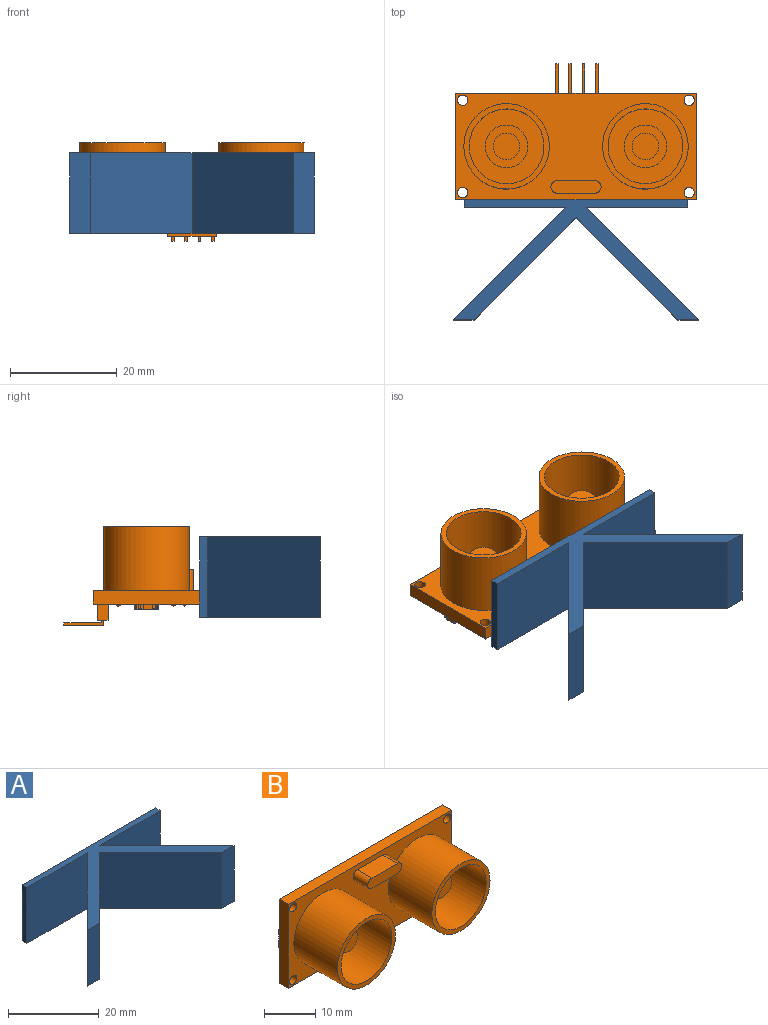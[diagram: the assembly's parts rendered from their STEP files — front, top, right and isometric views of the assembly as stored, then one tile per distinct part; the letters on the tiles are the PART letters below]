
ASSEMBLY  parts=2 mates=1
PART A: 13 faces, bbox 45.8x22.5x15.1 mm
  f0: plane 19.09x19.09mm, normal (0.71,-0.71,0), area 408mm2, adj f1,f10,f11,f12
  f1: plane 19.09x19.09mm, normal (-0.71,-0.71,0), area 408mm2, adj f0,f2,f11,f12
  f2: plane 15.11x3.82mm, normal (0,-1,0), area 57.7mm2, adj f1,f3,f11,f12
  f3: plane 21x21mm, normal (0.71,0.71,0), area 448.8mm2, adj f2,f4,f11,f12
  f4: plane 18.94x15.11mm, normal (0,-1,0), area 286.2mm2, adj f3,f5,f11,f12
  f5: plane 15.11x1.5mm, normal (1,0,0), area 22.7mm2, adj f4,f6,f11,f12
  f6: plane 41.7x15.11mm, normal (0,1,0), area 630.1mm2, adj f5,f7,f11,f12
  f7: plane 15.11x1.5mm, normal (-1,0,0), area 22.7mm2, adj f6,f8,f11,f12
  f8: plane 18.94x15.11mm, normal (0,-1,0), area 286.2mm2, adj f7,f9,f11,f12
  f9: plane 21x21mm, normal (-0.71,0.71,0), area 448.8mm2, adj f8,f10,f11,f12
  f10: plane 15.11x3.82mm, normal (0,-1,0), area 57.7mm2, adj f0,f9,f11,f12
  f11: plane 45.82x22.5mm, normal (0,0,1), area 219.3mm2, adj f0,f1,f2,f3,f4,f5,f6,f7
  f12: plane 45.82x22.5mm, normal (0,0,-1), area 219.3mm2, adj f0,f1,f2,f3,f4,f5,f6,f7
PART B: 331 faces, bbox 45x18.5x25.5 mm
  f0: plane 0.5x0.49mm, normal (0,0,-1), area 0.2mm2, adj f4,f319,f321,f329
  f1: plane 0.5x0.49mm, normal (0,0,-1), area 0.2mm2, adj f4,f315,f317,f327
  f2: plane 0.5x0.49mm, normal (0,0,-1), area 0.2mm2, adj f4,f311,f313,f325
  f3: plane 0.5x0.49mm, normal (0,0,-1), area 0.2mm2, adj f4,f307,f309,f323
  f4: plane 9x2mm, normal (0,1,0), area 17mm2, adj f0,f1,f2,f3,f303,f304,f305,f306
  f5: plane 45x20mm, normal (0,1,0), area 819.7mm2, adj f6,f7,f8,f9,f10,f11,f13,f14
  f6: plane 4.63x1mm, normal (1,0,0), area 3.2mm2, adj f5,f48,f49,f50,f235,f237,f238,f243
  f7: plane 4.63x1mm, normal (-1,0,0), area 3.2mm2, adj f5,f48,f49,f50,f232,f233,f234,f240
  f8: plane 5.79x1mm, normal (0,0,-1), area 4mm2, adj f5,f45,f46,f47,f147,f149,f150,f155
  f9: plane 5.79x1mm, normal (0,0,1), area 4mm2, adj f5,f45,f46,f47,f143,f144,f146,f151
  f10: plane 5.11x1mm, normal (0,0,-1), area 3.6mm2, adj f5,f42,f43,f44,f67,f70,f76,f77
  f11: plane 5.11x1mm, normal (0,0,1), area 3.6mm2, adj f5,f42,f43,f44,f62,f65,f71,f73
  f12: plane 45x20mm, normal (0,-1,0), area 464.5mm2, adj f13,f14,f15,f16,f17,f19,f33,f34
  f13: plane 20x2.5mm, normal (1,0,0), area 50mm2, adj f5,f12,f14,f16
  f14: plane 45x2.5mm, normal (0,0,1), area 112.5mm2, adj f5,f12,f13,f15
  f15: plane 20x2.5mm, normal (-1,0,0), area 50mm2, adj f5,f12,f14,f16
  f16: plane 45x2.5mm, normal (0,0,-1), area 112.5mm2, adj f5,f12,f13,f15
  f17: cylinder r=8mm len=16mm, axis (0,1,0), area 603.2mm2, adj f12,f18
  f18: plane 16x16mm, normal (0,-1,0), area 47.1mm2, adj f17,f23
  f19: cylinder r=8mm len=16mm, axis (0,1,0), area 603.2mm2, adj f12,f20
  f20: plane 16x16mm, normal (0,-1,0), area 47.1mm2, adj f19,f21
  f21: cylinder r=7mm len=14mm, axis (0,-1,0), area 527.8mm2, adj f20,f22
  f22: plane 14x14mm, normal (0,-1,0), area 103.7mm2, adj f21,f27
  f23: cylinder r=7mm len=14mm, axis (0,-1,0), area 527.8mm2, adj f18,f24
  f24: plane 14x14mm, normal (0,-1,0), area 103.7mm2, adj f23,f25
  f25: cylinder r=4mm len=8mm, axis (0,1,0), area 125.7mm2, adj f24,f26
  f26: plane 8x8mm, normal (0,-1,0), area 30.6mm2, adj f25,f29
  f27: cylinder r=4mm len=8mm, axis (0,1,0), area 125.7mm2, adj f22,f28
  f28: plane 8x8mm, normal (0,-1,0), area 30.6mm2, adj f27,f31
  f29: cylinder r=2.5mm len=5mm, axis (0,1,0), area 31.4mm2, adj f26,f30
  f30: plane 5x5mm, normal (0,-1,0), area 19.6mm2, adj f29
  f31: cylinder r=2.5mm len=5mm, axis (0,1,0), area 31.4mm2, adj f28,f32
  f32: plane 5x5mm, normal (0,-1,0), area 19.6mm2, adj f31
  f33: cylinder r=0.97mm len=2.5mm, axis (0,-1,0), area 15.3mm2, adj f5,f12
  f34: cylinder r=0.97mm len=2.5mm, axis (0,-1,0), area 15.3mm2, adj f5,f12
  f35: cylinder r=0.97mm len=2.5mm, axis (0,-1,0), area 15.3mm2, adj f5,f12
  f36: cylinder r=0.97mm len=2.5mm, axis (0,-1,0), area 15.3mm2, adj f5,f12
  f37: cylinder r=1.2mm len=4mm, axis (0,1,0), area 15.1mm2, adj f12,f38,f40,f41
  f38: plane 7x4mm, normal (0,0,-1), area 28mm2, adj f12,f37,f39,f41
  f39: cylinder r=1.2mm len=4mm, axis (0,1,0), area 15.1mm2, adj f12,f38,f40,f41
  f40: plane 7x4mm, normal (0,0,1), area 28mm2, adj f12,f37,f39,f41
  f41: plane 9.41x2.41mm, normal (0,-1,0), area 21.4mm2, adj f37,f38,f39,f40
  f42: plane 1.79x1mm, normal (-1,0,0), area 1.8mm2, adj f5,f10,f11,f44
  f43: plane 1.79x1mm, normal (1,0,0), area 1.8mm2, adj f5,f10,f11,f44,f61,f66
  f44: plane 5.11x1.79mm, normal (0,1,0), area 9.2mm2, adj f10,f11,f42,f43
  f45: plane 1.93x1mm, normal (-1,0,0), area 1.9mm2, adj f5,f8,f9,f47
  f46: plane 1.93x1mm, normal (1,0,0), area 1.9mm2, adj f5,f8,f9,f47
  f47: plane 5.79x1.93mm, normal (0,1,0), area 11.2mm2, adj f8,f9,f45,f46
  f48: plane 2.12x1mm, normal (0,0,1), area 2.1mm2, adj f5,f6,f7,f50
  f49: plane 2.12x1mm, normal (0,0,-1), area 2.1mm2, adj f5,f6,f7,f50
  f50: plane 4.63x2.12mm, normal (0,1,0), area 9.8mm2, adj f6,f7,f48,f49
  f51: cone r=1mm half-angle=62deg, axis (0,-1,0), area 3.5mm2, adj f5,f52
  f52: plane 0.12x0.12mm, normal (0,1,0), area 0mm2, adj f51
  f53: cone r=1mm half-angle=62deg, axis (0,-1,0), area 3.5mm2, adj f5,f54
  f54: plane 0.12x0.12mm, normal (0,1,0), area 0mm2, adj f53
  f55: cone r=1mm half-angle=62deg, axis (0,-1,0), area 3.5mm2, adj f5,f56
  f56: plane 0.12x0.12mm, normal (0,1,0), area 0mm2, adj f55
  f57: cone r=1mm half-angle=62deg, axis (0,-1,0), area 3.5mm2, adj f5,f58
  f58: plane 0.12x0.12mm, normal (0,1,0), area 0mm2, adj f57
  f59: cone r=0.5mm half-angle=45deg, axis (0,-1,0), area 1.1mm2, adj f5
  f60: cone r=0.5mm half-angle=45deg, axis (0,-1,0), area 1.1mm2, adj f5
  f61: plane 0.8x0.12mm, normal (0,0,-1), area 0.1mm2, adj f5,f43,f63,f65
  f62: plane 0.8x0.5mm, normal (-1,0,0), area 0.4mm2, adj f5,f11,f64,f65
  f63: plane 0.8x0.5mm, normal (1,0,0), area 0.4mm2, adj f5,f61,f64,f65
  f64: plane 0.8x0.2mm, normal (0,0,1), area 0.2mm2, adj f5,f62,f63,f65
  f65: plane 0.5x0.2mm, normal (0,1,0), area 0.1mm2, adj f11,f61,f62,f63,f64
  f66: plane 0.8x0.12mm, normal (0,0,1), area 0.1mm2, adj f5,f43,f69,f70
  f67: plane 0.8x0.5mm, normal (-1,0,0), area 0.4mm2, adj f5,f10,f68,f70
  f68: plane 0.8x0.2mm, normal (0,0,-1), area 0.2mm2, adj f5,f67,f69,f70
  f69: plane 0.8x0.5mm, normal (1,0,0), area 0.4mm2, adj f5,f66,f68,f70
  f70: plane 0.5x0.2mm, normal (0,1,0), area 0.1mm2, adj f10,f66,f67,f68,f69
  f71: plane 0.8x0.5mm, normal (1,0,0), area 0.4mm2, adj f5,f11,f72,f74
  f72: plane 0.8x0.2mm, normal (0,0,1), area 0.2mm2, adj f5,f71,f73,f74
  f73: plane 0.8x0.5mm, normal (-1,0,0), area 0.4mm2, adj f5,f11,f72,f74
  f74: plane 0.5x0.2mm, normal (0,1,0), area 0.1mm2, adj f11,f71,f72,f73
  f75: plane 0.8x0.2mm, normal (0,0,-1), area 0.2mm2, adj f5,f76,f77,f78
  f76: plane 0.8x0.5mm, normal (1,0,0), area 0.4mm2, adj f5,f10,f75,f78
  f77: plane 0.8x0.5mm, normal (-1,0,0), area 0.4mm2, adj f5,f10,f75,f78
  f78: plane 0.5x0.2mm, normal (0,1,0), area 0.1mm2, adj f10,f75,f76,f77
  f79: plane 0.8x0.5mm, normal (1,0,0), area 0.4mm2, adj f5,f11,f80,f82
  f80: plane 0.8x0.2mm, normal (0,0,1), area 0.2mm2, adj f5,f79,f81,f82
  f81: plane 0.8x0.5mm, normal (-1,0,0), area 0.4mm2, adj f5,f11,f80,f82
  f82: plane 0.5x0.2mm, normal (0,1,0), area 0.1mm2, adj f11,f79,f80,f81
  f83: plane 0.8x0.2mm, normal (0,0,-1), area 0.2mm2, adj f5,f84,f85,f86
  f84: plane 0.8x0.5mm, normal (1,0,0), area 0.4mm2, adj f5,f10,f83,f86
  f85: plane 0.8x0.5mm, normal (-1,0,0), area 0.4mm2, adj f5,f10,f83,f86
  f86: plane 0.5x0.2mm, normal (0,1,0), area 0.1mm2, adj f10,f83,f84,f85
  f87: plane 0.8x0.5mm, normal (1,0,0), area 0.4mm2, adj f5,f11,f88,f90
  f88: plane 0.8x0.2mm, normal (0,0,1), area 0.2mm2, adj f5,f87,f89,f90
  f89: plane 0.8x0.5mm, normal (-1,0,0), area 0.4mm2, adj f5,f11,f88,f90
  f90: plane 0.5x0.2mm, normal (0,1,0), area 0.1mm2, adj f11,f87,f88,f89
  f91: plane 0.8x0.2mm, normal (0,0,-1), area 0.2mm2, adj f5,f92,f93,f94
  f92: plane 0.8x0.5mm, normal (1,0,0), area 0.4mm2, adj f5,f10,f91,f94
  f93: plane 0.8x0.5mm, normal (-1,0,0), area 0.4mm2, adj f5,f10,f91,f94
  f94: plane 0.5x0.2mm, normal (0,1,0), area 0.1mm2, adj f10,f91,f92,f93
  f95: plane 0.8x0.5mm, normal (1,0,0), area 0.4mm2, adj f5,f11,f96,f98
  f96: plane 0.8x0.2mm, normal (0,0,1), area 0.2mm2, adj f5,f95,f97,f98
  f97: plane 0.8x0.5mm, normal (-1,0,0), area 0.4mm2, adj f5,f11,f96,f98
  f98: plane 0.5x0.2mm, normal (0,1,0), area 0.1mm2, adj f11,f95,f96,f97
  f99: plane 0.8x0.2mm, normal (0,0,-1), area 0.2mm2, adj f5,f100,f101,f102
  f100: plane 0.8x0.5mm, normal (1,0,0), area 0.4mm2, adj f5,f10,f99,f102
  f101: plane 0.8x0.5mm, normal (-1,0,0), area 0.4mm2, adj f5,f10,f99,f102
  f102: plane 0.5x0.2mm, normal (0,1,0), area 0.1mm2, adj f10,f99,f100,f101
  f103: plane 0.8x0.5mm, normal (1,0,0), area 0.4mm2, adj f5,f11,f104,f106
  f104: plane 0.8x0.2mm, normal (0,0,1), area 0.2mm2, adj f5,f103,f105,f106
  f105: plane 0.8x0.5mm, normal (-1,0,0), area 0.4mm2, adj f5,f11,f104,f106
  f106: plane 0.5x0.2mm, normal (0,1,0), area 0.1mm2, adj f11,f103,f104,f105
  f107: plane 0.8x0.2mm, normal (0,0,-1), area 0.2mm2, adj f5,f108,f109,f110
  f108: plane 0.8x0.5mm, normal (1,0,0), area 0.4mm2, adj f5,f10,f107,f110
  f109: plane 0.8x0.5mm, normal (-1,0,0), area 0.4mm2, adj f5,f10,f107,f110
  f110: plane 0.5x0.2mm, normal (0,1,0), area 0.1mm2, adj f10,f107,f108,f109
  f111: plane 0.8x0.5mm, normal (1,0,0), area 0.4mm2, adj f5,f11,f112,f114
  f112: plane 0.8x0.2mm, normal (0,0,1), area 0.2mm2, adj f5,f111,f113,f114
  f113: plane 0.8x0.5mm, normal (-1,0,0), area 0.4mm2, adj f5,f11,f112,f114
  f114: plane 0.5x0.2mm, normal (0,1,0), area 0.1mm2, adj f11,f111,f112,f113
  f115: plane 0.8x0.2mm, normal (0,0,-1), area 0.2mm2, adj f5,f116,f117,f118
  f116: plane 0.8x0.5mm, normal (1,0,0), area 0.4mm2, adj f5,f10,f115,f118
  f117: plane 0.8x0.5mm, normal (-1,0,0), area 0.4mm2, adj f5,f10,f115,f118
  f118: plane 0.5x0.2mm, normal (0,1,0), area 0.1mm2, adj f10,f115,f116,f117
  f119: plane 0.8x0.5mm, normal (1,0,0), area 0.4mm2, adj f5,f11,f120,f122
  f120: plane 0.8x0.2mm, normal (0,0,1), area 0.2mm2, adj f5,f119,f121,f122
  f121: plane 0.8x0.5mm, normal (-1,0,0), area 0.4mm2, adj f5,f11,f120,f122
  f122: plane 0.5x0.2mm, normal (0,1,0), area 0.1mm2, adj f11,f119,f120,f121
  f123: plane 0.8x0.2mm, normal (0,0,-1), area 0.2mm2, adj f5,f124,f125,f126
  f124: plane 0.8x0.5mm, normal (1,0,0), area 0.4mm2, adj f5,f10,f123,f126
  f125: plane 0.8x0.5mm, normal (-1,0,0), area 0.4mm2, adj f5,f10,f123,f126
  f126: plane 0.5x0.2mm, normal (0,1,0), area 0.1mm2, adj f10,f123,f124,f125
  f127: plane 0.8x0.5mm, normal (1,0,0), area 0.4mm2, adj f5,f11,f128,f130
  f128: plane 0.8x0.2mm, normal (0,0,1), area 0.2mm2, adj f5,f127,f129,f130
  f129: plane 0.8x0.5mm, normal (-1,0,0), area 0.4mm2, adj f5,f11,f128,f130
  f130: plane 0.5x0.2mm, normal (0,1,0), area 0.1mm2, adj f11,f127,f128,f129
  f131: plane 0.8x0.2mm, normal (0,0,-1), area 0.2mm2, adj f5,f132,f133,f134
  f132: plane 0.8x0.5mm, normal (1,0,0), area 0.4mm2, adj f5,f10,f131,f134
  f133: plane 0.8x0.5mm, normal (-1,0,0), area 0.4mm2, adj f5,f10,f131,f134
  f134: plane 0.5x0.2mm, normal (0,1,0), area 0.1mm2, adj f10,f131,f132,f133
  f135: plane 0.8x0.5mm, normal (1,0,0), area 0.4mm2, adj f5,f11,f136,f138
  f136: plane 0.8x0.2mm, normal (0,0,1), area 0.2mm2, adj f5,f135,f137,f138
  f137: plane 0.8x0.5mm, normal (-1,0,0), area 0.4mm2, adj f5,f11,f136,f138
  f138: plane 0.5x0.2mm, normal (0,1,0), area 0.1mm2, adj f11,f135,f136,f137
  f139: plane 0.8x0.2mm, normal (0,0,-1), area 0.2mm2, adj f5,f140,f141,f142
  f140: plane 0.8x0.5mm, normal (1,0,0), area 0.4mm2, adj f5,f10,f139,f142
  f141: plane 0.8x0.5mm, normal (-1,0,0), area 0.4mm2, adj f5,f10,f139,f142
  f142: plane 0.5x0.2mm, normal (0,1,0), area 0.1mm2, adj f10,f139,f140,f141
  f143: plane 0.8x0.5mm, normal (-1,0,0), area 0.4mm2, adj f5,f9,f145,f146
  f144: plane 0.8x0.5mm, normal (1,0,0), area 0.4mm2, adj f5,f9,f145,f146
  f145: plane 0.8x0.2mm, normal (0,0,1), area 0.2mm2, adj f5,f143,f144,f146
  f146: plane 0.5x0.2mm, normal (0,1,0), area 0.1mm2, adj f9,f143,f144,f145
  f147: plane 0.8x0.5mm, normal (-1,0,0), area 0.4mm2, adj f5,f8,f148,f150
  f148: plane 0.8x0.2mm, normal (0,0,-1), area 0.2mm2, adj f5,f147,f149,f150
  f149: plane 0.8x0.5mm, normal (1,0,0), area 0.4mm2, adj f5,f8,f148,f150
  f150: plane 0.5x0.2mm, normal (0,1,0), area 0.1mm2, adj f8,f147,f148,f149
  f151: plane 0.8x0.5mm, normal (1,0,0), area 0.4mm2, adj f5,f9,f152,f154
  f152: plane 0.8x0.2mm, normal (0,0,1), area 0.2mm2, adj f5,f151,f153,f154
  f153: plane 0.8x0.5mm, normal (-1,0,0), area 0.4mm2, adj f5,f9,f152,f154
  f154: plane 0.5x0.2mm, normal (0,1,0), area 0.1mm2, adj f9,f151,f152,f153
  f155: plane 0.8x0.5mm, normal (-1,0,0), area 0.4mm2, adj f5,f8,f156,f158
  f156: plane 0.8x0.2mm, normal (0,0,-1), area 0.2mm2, adj f5,f155,f157,f158
  f157: plane 0.8x0.5mm, normal (1,0,0), area 0.4mm2, adj f5,f8,f156,f158
  f158: plane 0.5x0.2mm, normal (0,1,0), area 0.1mm2, adj f8,f155,f156,f157
  f159: plane 0.8x0.5mm, normal (1,0,0), area 0.4mm2, adj f5,f9,f160,f162
  f160: plane 0.8x0.2mm, normal (0,0,1), area 0.2mm2, adj f5,f159,f161,f162
  f161: plane 0.8x0.5mm, normal (-1,0,0), area 0.4mm2, adj f5,f9,f160,f162
  f162: plane 0.5x0.2mm, normal (0,1,0), area 0.1mm2, adj f9,f159,f160,f161
  f163: plane 0.8x0.5mm, normal (-1,0,0), area 0.4mm2, adj f5,f8,f164,f166
  f164: plane 0.8x0.2mm, normal (0,0,-1), area 0.2mm2, adj f5,f163,f165,f166
  f165: plane 0.8x0.5mm, normal (1,0,0), area 0.4mm2, adj f5,f8,f164,f166
  f166: plane 0.5x0.2mm, normal (0,1,0), area 0.1mm2, adj f8,f163,f164,f165
  f167: plane 0.8x0.5mm, normal (1,0,0), area 0.4mm2, adj f5,f9,f168,f170
  f168: plane 0.8x0.2mm, normal (0,0,1), area 0.2mm2, adj f5,f167,f169,f170
  f169: plane 0.8x0.5mm, normal (-1,0,0), area 0.4mm2, adj f5,f9,f168,f170
  f170: plane 0.5x0.2mm, normal (0,1,0), area 0.1mm2, adj f9,f167,f168,f169
  f171: plane 0.8x0.5mm, normal (-1,0,0), area 0.4mm2, adj f5,f8,f172,f174
  f172: plane 0.8x0.2mm, normal (0,0,-1), area 0.2mm2, adj f5,f171,f173,f174
  f173: plane 0.8x0.5mm, normal (1,0,0), area 0.4mm2, adj f5,f8,f172,f174
  f174: plane 0.5x0.2mm, normal (0,1,0), area 0.1mm2, adj f8,f171,f172,f173
  f175: plane 0.8x0.5mm, normal (1,0,0), area 0.4mm2, adj f5,f9,f176,f178
  f176: plane 0.8x0.2mm, normal (0,0,1), area 0.2mm2, adj f5,f175,f177,f178
  f177: plane 0.8x0.5mm, normal (-1,0,0), area 0.4mm2, adj f5,f9,f176,f178
  f178: plane 0.5x0.2mm, normal (0,1,0), area 0.1mm2, adj f9,f175,f176,f177
  f179: plane 0.8x0.5mm, normal (-1,0,0), area 0.4mm2, adj f5,f8,f180,f182
  f180: plane 0.8x0.2mm, normal (0,0,-1), area 0.2mm2, adj f5,f179,f181,f182
  f181: plane 0.8x0.5mm, normal (1,0,0), area 0.4mm2, adj f5,f8,f180,f182
  f182: plane 0.5x0.2mm, normal (0,1,0), area 0.1mm2, adj f8,f179,f180,f181
  f183: plane 0.8x0.5mm, normal (1,0,0), area 0.4mm2, adj f5,f9,f184,f186
  f184: plane 0.8x0.2mm, normal (0,0,1), area 0.2mm2, adj f5,f183,f185,f186
  f185: plane 0.8x0.5mm, normal (-1,0,0), area 0.4mm2, adj f5,f9,f184,f186
  f186: plane 0.5x0.2mm, normal (0,1,0), area 0.1mm2, adj f9,f183,f184,f185
  f187: plane 0.8x0.5mm, normal (-1,0,0), area 0.4mm2, adj f5,f8,f188,f190
  f188: plane 0.8x0.2mm, normal (0,0,-1), area 0.2mm2, adj f5,f187,f189,f190
  f189: plane 0.8x0.5mm, normal (1,0,0), area 0.4mm2, adj f5,f8,f188,f190
  f190: plane 0.5x0.2mm, normal (0,1,0), area 0.1mm2, adj f8,f187,f188,f189
  f191: plane 0.8x0.5mm, normal (1,0,0), area 0.4mm2, adj f5,f9,f192,f194
  f192: plane 0.8x0.2mm, normal (0,0,1), area 0.2mm2, adj f5,f191,f193,f194
  f193: plane 0.8x0.5mm, normal (-1,0,0), area 0.4mm2, adj f5,f9,f192,f194
  f194: plane 0.5x0.2mm, normal (0,1,0), area 0.1mm2, adj f9,f191,f192,f193
  f195: plane 0.8x0.5mm, normal (-1,0,0), area 0.4mm2, adj f5,f8,f196,f198
  f196: plane 0.8x0.2mm, normal (0,0,-1), area 0.2mm2, adj f5,f195,f197,f198
  f197: plane 0.8x0.5mm, normal (1,0,0), area 0.4mm2, adj f5,f8,f196,f198
  f198: plane 0.5x0.2mm, normal (0,1,0), area 0.1mm2, adj f8,f195,f196,f197
  f199: plane 0.8x0.5mm, normal (1,0,0), area 0.4mm2, adj f5,f9,f200,f202
  f200: plane 0.8x0.2mm, normal (0,0,1), area 0.2mm2, adj f5,f199,f201,f202
  f201: plane 0.8x0.5mm, normal (-1,0,0), area 0.4mm2, adj f5,f9,f200,f202
  f202: plane 0.5x0.2mm, normal (0,1,0), area 0.1mm2, adj f9,f199,f200,f201
  f203: plane 0.8x0.5mm, normal (-1,0,0), area 0.4mm2, adj f5,f8,f204,f206
  f204: plane 0.8x0.2mm, normal (0,0,-1), area 0.2mm2, adj f5,f203,f205,f206
  f205: plane 0.8x0.5mm, normal (1,0,0), area 0.4mm2, adj f5,f8,f204,f206
  f206: plane 0.5x0.2mm, normal (0,1,0), area 0.1mm2, adj f8,f203,f204,f205
  f207: plane 0.8x0.5mm, normal (1,0,0), area 0.4mm2, adj f5,f9,f208,f210
  f208: plane 0.8x0.2mm, normal (0,0,1), area 0.2mm2, adj f5,f207,f209,f210
  f209: plane 0.8x0.5mm, normal (-1,0,0), area 0.4mm2, adj f5,f9,f208,f210
  f210: plane 0.5x0.2mm, normal (0,1,0), area 0.1mm2, adj f9,f207,f208,f209
  f211: plane 0.8x0.5mm, normal (-1,0,0), area 0.4mm2, adj f5,f8,f212,f214
  f212: plane 0.8x0.2mm, normal (0,0,-1), area 0.2mm2, adj f5,f211,f213,f214
  f213: plane 0.8x0.5mm, normal (1,0,0), area 0.4mm2, adj f5,f8,f212,f214
  f214: plane 0.5x0.2mm, normal (0,1,0), area 0.1mm2, adj f8,f211,f212,f213
  f215: plane 0.8x0.5mm, normal (1,0,0), area 0.4mm2, adj f5,f9,f216,f218
  f216: plane 0.8x0.2mm, normal (0,0,1), area 0.2mm2, adj f5,f215,f217,f218
  f217: plane 0.8x0.5mm, normal (-1,0,0), area 0.4mm2, adj f5,f9,f216,f218
  f218: plane 0.5x0.2mm, normal (0,1,0), area 0.1mm2, adj f9,f215,f216,f217
  f219: plane 0.8x0.5mm, normal (-1,0,0), area 0.4mm2, adj f5,f8,f220,f222
  f220: plane 0.8x0.2mm, normal (0,0,-1), area 0.2mm2, adj f5,f219,f221,f222
  f221: plane 0.8x0.5mm, normal (1,0,0), area 0.4mm2, adj f5,f8,f220,f222
  f222: plane 0.5x0.2mm, normal (0,1,0), area 0.1mm2, adj f8,f219,f220,f221
  f223: plane 0.8x0.5mm, normal (1,0,0), area 0.4mm2, adj f5,f9,f224,f226
  f224: plane 0.8x0.2mm, normal (0,0,1), area 0.2mm2, adj f5,f223,f225,f226
  f225: plane 0.8x0.5mm, normal (-1,0,0), area 0.4mm2, adj f5,f9,f224,f226
  f226: plane 0.5x0.2mm, normal (0,1,0), area 0.1mm2, adj f9,f223,f224,f225
  f227: plane 0.8x0.5mm, normal (-1,0,0), area 0.4mm2, adj f5,f8,f228,f230
  f228: plane 0.8x0.2mm, normal (0,0,-1), area 0.2mm2, adj f5,f227,f229,f230
  f229: plane 0.8x0.5mm, normal (1,0,0), area 0.4mm2, adj f5,f8,f228,f230
  f230: plane 0.5x0.2mm, normal (0,1,0), area 0.1mm2, adj f8,f227,f228,f229
  f231: plane 0.8x0.2mm, normal (-1,0,0), area 0.2mm2, adj f5,f232,f233,f234
  f232: plane 0.8x0.54mm, normal (0,0,-1), area 0.4mm2, adj f5,f7,f231,f234
  f233: plane 0.8x0.54mm, normal (0,0,1), area 0.4mm2, adj f5,f7,f231,f234
  f234: plane 0.54x0.2mm, normal (0,1,0), area 0.1mm2, adj f7,f231,f232,f233
  f235: plane 0.8x0.5mm, normal (0,0,-1), area 0.4mm2, adj f5,f6,f236,f238
  f236: plane 0.8x0.2mm, normal (1,0,0), area 0.2mm2, adj f5,f235,f237,f238
  f237: plane 0.8x0.5mm, normal (0,0,1), area 0.4mm2, adj f5,f6,f236,f238
  f238: plane 0.5x0.2mm, normal (0,1,0), area 0.1mm2, adj f6,f235,f236,f237
  f239: plane 0.8x0.2mm, normal (-1,0,0), area 0.2mm2, adj f5,f240,f241,f242
  f240: plane 0.8x0.54mm, normal (0,0,-1), area 0.4mm2, adj f5,f7,f239,f242
  f241: plane 0.8x0.54mm, normal (0,0,1), area 0.4mm2, adj f5,f7,f239,f242
  f242: plane 0.54x0.2mm, normal (0,1,0), area 0.1mm2, adj f7,f239,f240,f241
  f243: plane 0.8x0.5mm, normal (0,0,-1), area 0.4mm2, adj f5,f6,f244,f246
  f244: plane 0.8x0.2mm, normal (1,0,0), area 0.2mm2, adj f5,f243,f245,f246
  f245: plane 0.8x0.5mm, normal (0,0,1), area 0.4mm2, adj f5,f6,f244,f246
  f246: plane 0.5x0.2mm, normal (0,1,0), area 0.1mm2, adj f6,f243,f244,f245
  f247: plane 0.8x0.2mm, normal (-1,0,0), area 0.2mm2, adj f5,f248,f249,f250
  f248: plane 0.8x0.54mm, normal (0,0,-1), area 0.4mm2, adj f5,f7,f247,f250
  f249: plane 0.8x0.54mm, normal (0,0,1), area 0.4mm2, adj f5,f7,f247,f250
  f250: plane 0.54x0.2mm, normal (0,1,0), area 0.1mm2, adj f7,f247,f248,f249
  f251: plane 0.8x0.5mm, normal (0,0,-1), area 0.4mm2, adj f5,f6,f252,f254
  f252: plane 0.8x0.2mm, normal (1,0,0), area 0.2mm2, adj f5,f251,f253,f254
  f253: plane 0.8x0.5mm, normal (0,0,1), area 0.4mm2, adj f5,f6,f252,f254
  f254: plane 0.5x0.2mm, normal (0,1,0), area 0.1mm2, adj f6,f251,f252,f253
  f255: plane 0.8x0.2mm, normal (-1,0,0), area 0.2mm2, adj f5,f256,f257,f258
  f256: plane 0.8x0.54mm, normal (0,0,-1), area 0.4mm2, adj f5,f7,f255,f258
  f257: plane 0.8x0.54mm, normal (0,0,1), area 0.4mm2, adj f5,f7,f255,f258
  f258: plane 0.54x0.2mm, normal (0,1,0), area 0.1mm2, adj f7,f255,f256,f257
  f259: plane 0.8x0.5mm, normal (0,0,-1), area 0.4mm2, adj f5,f6,f260,f262
  f260: plane 0.8x0.2mm, normal (1,0,0), area 0.2mm2, adj f5,f259,f261,f262
  f261: plane 0.8x0.5mm, normal (0,0,1), area 0.4mm2, adj f5,f6,f260,f262
  f262: plane 0.5x0.2mm, normal (0,1,0), area 0.1mm2, adj f6,f259,f260,f261
  f263: plane 0.8x0.2mm, normal (-1,0,0), area 0.2mm2, adj f5,f264,f265,f266
  f264: plane 0.8x0.54mm, normal (0,0,-1), area 0.4mm2, adj f5,f7,f263,f266
  f265: plane 0.8x0.54mm, normal (0,0,1), area 0.4mm2, adj f5,f7,f263,f266
  f266: plane 0.54x0.2mm, normal (0,1,0), area 0.1mm2, adj f7,f263,f264,f265
  f267: plane 0.8x0.5mm, normal (0,0,-1), area 0.4mm2, adj f5,f6,f268,f270
  f268: plane 0.8x0.2mm, normal (1,0,0), area 0.2mm2, adj f5,f267,f269,f270
  f269: plane 0.8x0.5mm, normal (0,0,1), area 0.4mm2, adj f5,f6,f268,f270
  f270: plane 0.5x0.2mm, normal (0,1,0), area 0.1mm2, adj f6,f267,f268,f269
  f271: plane 0.8x0.2mm, normal (-1,0,0), area 0.2mm2, adj f5,f272,f273,f274
  f272: plane 0.8x0.54mm, normal (0,0,-1), area 0.4mm2, adj f5,f7,f271,f274
  f273: plane 0.8x0.54mm, normal (0,0,1), area 0.4mm2, adj f5,f7,f271,f274
  f274: plane 0.54x0.2mm, normal (0,1,0), area 0.1mm2, adj f7,f271,f272,f273
  f275: plane 0.8x0.5mm, normal (0,0,-1), area 0.4mm2, adj f5,f6,f276,f278
  f276: plane 0.8x0.2mm, normal (1,0,0), area 0.2mm2, adj f5,f275,f277,f278
  f277: plane 0.8x0.5mm, normal (0,0,1), area 0.4mm2, adj f5,f6,f276,f278
  f278: plane 0.5x0.2mm, normal (0,1,0), area 0.1mm2, adj f6,f275,f276,f277
  f279: plane 0.8x0.2mm, normal (-1,0,0), area 0.2mm2, adj f5,f280,f281,f282
  f280: plane 0.8x0.54mm, normal (0,0,-1), area 0.4mm2, adj f5,f7,f279,f282
  f281: plane 0.8x0.54mm, normal (0,0,1), area 0.4mm2, adj f5,f7,f279,f282
  f282: plane 0.54x0.2mm, normal (0,1,0), area 0.1mm2, adj f7,f279,f280,f281
  f283: plane 0.8x0.5mm, normal (0,0,-1), area 0.4mm2, adj f5,f6,f284,f286
  f284: plane 0.8x0.2mm, normal (1,0,0), area 0.2mm2, adj f5,f283,f285,f286
  f285: plane 0.8x0.5mm, normal (0,0,1), area 0.4mm2, adj f5,f6,f284,f286
  f286: plane 0.5x0.2mm, normal (0,1,0), area 0.1mm2, adj f6,f283,f284,f285
  f287: plane 0.8x0.2mm, normal (-1,0,0), area 0.2mm2, adj f5,f288,f289,f290
  f288: plane 0.8x0.54mm, normal (0,0,-1), area 0.4mm2, adj f5,f7,f287,f290
  f289: plane 0.8x0.54mm, normal (0,0,1), area 0.4mm2, adj f5,f7,f287,f290
  f290: plane 0.54x0.2mm, normal (0,1,0), area 0.1mm2, adj f7,f287,f288,f289
  f291: plane 0.8x0.5mm, normal (0,0,-1), area 0.4mm2, adj f5,f6,f292,f294
  f292: plane 0.8x0.2mm, normal (1,0,0), area 0.2mm2, adj f5,f291,f293,f294
  f293: plane 0.8x0.5mm, normal (0,0,1), area 0.4mm2, adj f5,f6,f292,f294
  f294: plane 0.5x0.2mm, normal (0,1,0), area 0.1mm2, adj f6,f291,f292,f293
  f295: plane 0.8x0.2mm, normal (-1,0,0), area 0.2mm2, adj f5,f296,f297,f298
  f296: plane 0.8x0.54mm, normal (0,0,-1), area 0.4mm2, adj f5,f7,f295,f298
  f297: plane 0.8x0.54mm, normal (0,0,1), area 0.4mm2, adj f5,f7,f295,f298
  f298: plane 0.54x0.2mm, normal (0,1,0), area 0.1mm2, adj f7,f295,f296,f297
  f299: plane 0.8x0.5mm, normal (0,0,-1), area 0.4mm2, adj f5,f6,f300,f302
  f300: plane 0.8x0.2mm, normal (1,0,0), area 0.2mm2, adj f5,f299,f301,f302
  f301: plane 0.8x0.5mm, normal (0,0,1), area 0.4mm2, adj f5,f6,f300,f302
  f302: plane 0.5x0.2mm, normal (0,1,0), area 0.1mm2, adj f6,f299,f300,f301
  f303: plane 3x2mm, normal (1,0,0), area 6mm2, adj f4,f5,f304,f306
  f304: plane 9x3mm, normal (0,0,-1), area 27mm2, adj f4,f5,f303,f305
  f305: plane 3x2mm, normal (-1,0,0), area 6mm2, adj f4,f5,f304,f306
  f306: plane 9x3mm, normal (0,0,1), area 27mm2, adj f4,f5,f303,f305
  f307: plane 7.5x1mm, normal (-1,0,0), area 4.1mm2, adj f3,f4,f308,f310,f323,f324
  f308: plane 1x0.5mm, normal (0,0,1), area 0.5mm2, adj f4,f307,f309,f310
  f309: plane 7.5x1mm, normal (1,0,0), area 4.1mm2, adj f3,f4,f308,f310,f323,f324
  f310: plane 7.5x0.5mm, normal (0,1,0), area 3.8mm2, adj f307,f308,f309,f324
  f311: plane 7.5x1mm, normal (-1,0,0), area 4.1mm2, adj f2,f4,f312,f314,f325,f326
  f312: plane 1x0.5mm, normal (0,0,1), area 0.5mm2, adj f4,f311,f313,f314
  f313: plane 7.5x1mm, normal (1,0,0), area 4.1mm2, adj f2,f4,f312,f314,f325,f326
  f314: plane 7.5x0.5mm, normal (0,1,0), area 3.8mm2, adj f311,f312,f313,f326
  f315: plane 7.5x1mm, normal (-1,0,0), area 4.1mm2, adj f1,f4,f316,f318,f327,f328
  f316: plane 1x0.5mm, normal (0,0,1), area 0.5mm2, adj f4,f315,f317,f318
  f317: plane 7.5x1mm, normal (1,0,0), area 4.1mm2, adj f1,f4,f316,f318,f327,f328
  f318: plane 7.5x0.5mm, normal (0,1,0), area 3.8mm2, adj f315,f316,f317,f328
  f319: plane 7.5x1mm, normal (-1,0,0), area 4.1mm2, adj f0,f4,f320,f322,f329,f330
  f320: plane 1x0.5mm, normal (0,0,1), area 0.5mm2, adj f4,f319,f321,f322
  f321: plane 7.5x1mm, normal (1,0,0), area 4.1mm2, adj f0,f4,f320,f322,f329,f330
  f322: plane 7.5x0.5mm, normal (0,1,0), area 3.8mm2, adj f319,f320,f321,f330
  f323: plane 7x0.5mm, normal (0,-1,0), area 3.5mm2, adj f3,f307,f309,f324
  f324: plane 0.51x0.5mm, normal (0,0,-1), area 0.3mm2, adj f307,f309,f310,f323
  f325: plane 7x0.5mm, normal (0,-1,0), area 3.5mm2, adj f2,f311,f313,f326
  f326: plane 0.51x0.5mm, normal (0,0,-1), area 0.3mm2, adj f311,f313,f314,f325
  f327: plane 7x0.5mm, normal (0,-1,0), area 3.5mm2, adj f1,f315,f317,f328
  f328: plane 0.51x0.5mm, normal (0,0,-1), area 0.3mm2, adj f315,f317,f318,f327
  f329: plane 7x0.5mm, normal (0,-1,0), area 3.5mm2, adj f0,f319,f321,f330
  f330: plane 0.51x0.5mm, normal (0,0,-1), area 0.3mm2, adj f319,f321,f322,f329
PLACE A t=(-8.11,7.75,-0.67)mm
PLACE B rot(axis=(0,-0.71,0.71),180deg) t=(-8.11,21.15,1.85)mm
MATE fastened B.f14 <-> A.f6  axis (0,-1,0) through (-8.11,11.15,3.1)mm
